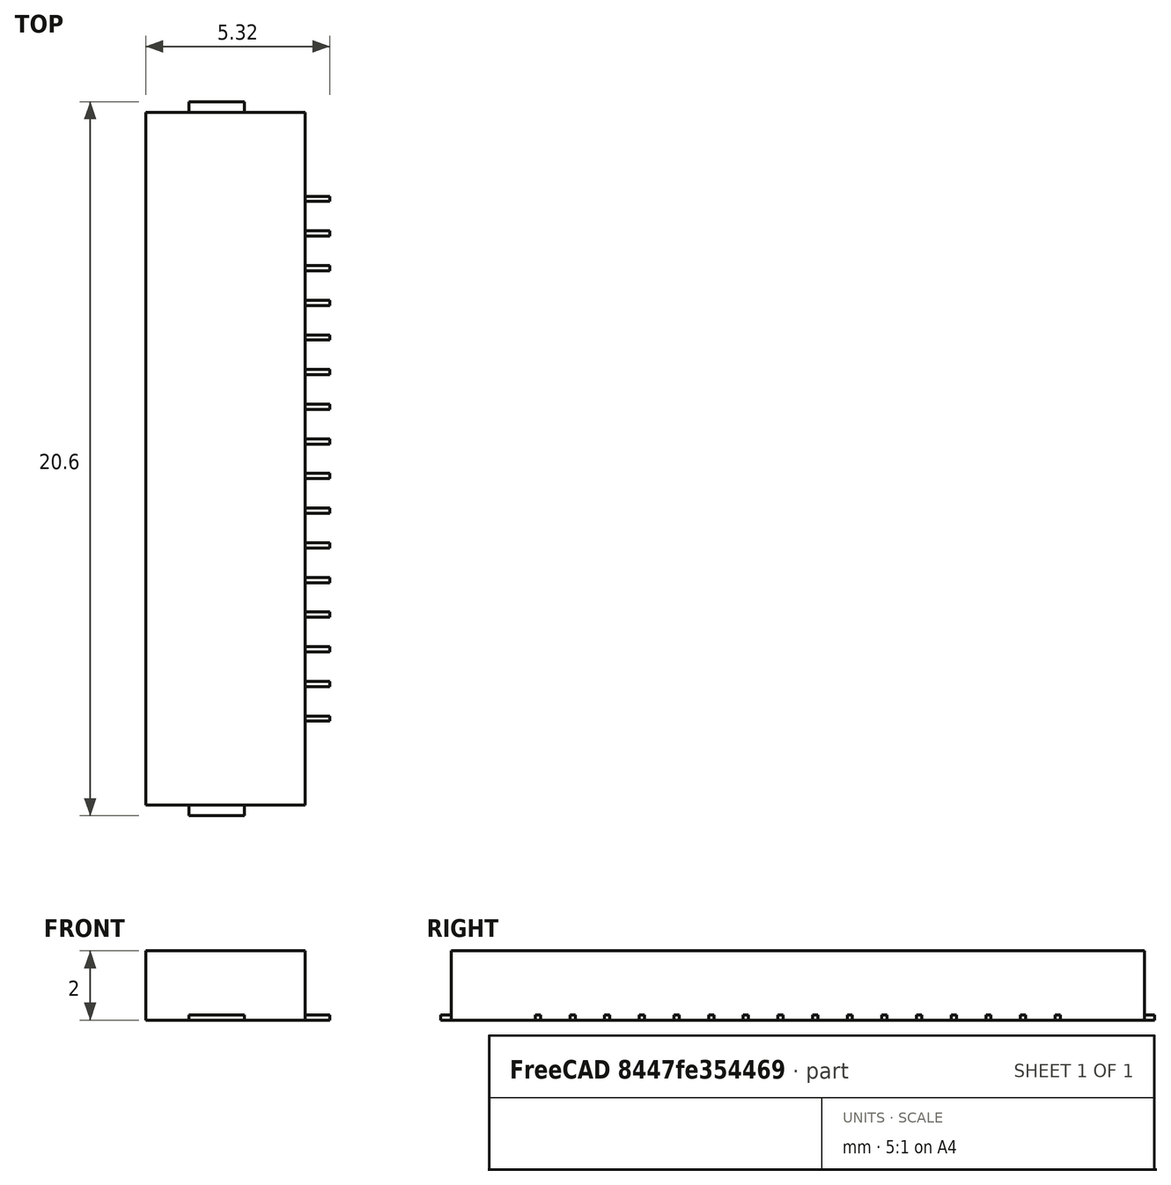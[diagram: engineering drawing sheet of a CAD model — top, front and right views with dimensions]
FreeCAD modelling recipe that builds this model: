
FCSTD DOCUMENT  (FreeCAD 0.20R29603 (Git))
Label: XFCN_F1004-H-16-20G-R
License: All rights reserved
LicenseURL: http://en.wikipedia.org/wiki/All_rights_reserved
objects: Part::Box×19
note: 19 computed .brp shape members not serialized (recipe doc carries the construction recipe); baked Part::Feature solids carry a one-line shape summary decoded from their .brp

FEATURE [Part::Box] Box  label="Body"
  AttacherType = Attacher::AttachEngine3D
  Height = 2
  Length = 4.6
  Width = 20
FEATURE [Part::Box] Box001  label="Pin 001"
  AttacherType = Attacher::AttachEngine3D
  Height = 0.15
  Length = 0.72
  Placement = pos=(4.6,17.425,0) rot=(0,0,1;0rad)
  Width = 0.15
FEATURE [Part::Box] Box002  label="Pin 002"
  AttacherType = Attacher::AttachEngine3D
  Height = 0.15
  Length = 0.72
  Placement = pos=(4.6,16.425,0) rot=(0,0,1;0rad)
  Width = 0.15
FEATURE [Part::Box] Box003  label="Pin 003"
  AttacherType = Attacher::AttachEngine3D
  Height = 0.15
  Length = 0.72
  Placement = pos=(4.6,15.425,0) rot=(0,0,1;0rad)
  Width = 0.15
FEATURE [Part::Box] Box004  label="Pin 004"
  AttacherType = Attacher::AttachEngine3D
  Height = 0.15
  Length = 0.72
  Placement = pos=(4.6,14.425,0) rot=(0,0,1;0rad)
  Width = 0.15
FEATURE [Part::Box] Box005  label="Pin 005"
  AttacherType = Attacher::AttachEngine3D
  Height = 0.15
  Length = 0.72
  Placement = pos=(4.6,13.425,0) rot=(0,0,1;0rad)
  Width = 0.15
FEATURE [Part::Box] Box006  label="Pin 006"
  AttacherType = Attacher::AttachEngine3D
  Height = 0.15
  Length = 0.72
  Placement = pos=(4.6,12.425,0) rot=(0,0,1;0rad)
  Width = 0.15
FEATURE [Part::Box] Box007  label="Pin 007"
  AttacherType = Attacher::AttachEngine3D
  Height = 0.15
  Length = 0.72
  Placement = pos=(4.6,11.425,0) rot=(0,0,1;0rad)
  Width = 0.15
FEATURE [Part::Box] Box008  label="Pin 008"
  AttacherType = Attacher::AttachEngine3D
  Height = 0.15
  Length = 0.72
  Placement = pos=(4.6,10.425,0) rot=(0,0,1;0rad)
  Width = 0.15
FEATURE [Part::Box] Box009  label="Pin 009"
  AttacherType = Attacher::AttachEngine3D
  Height = 0.15
  Length = 0.72
  Placement = pos=(4.6,9.425,0) rot=(0,0,1;0rad)
  Width = 0.15
FEATURE [Part::Box] Box010  label="Pin 010"
  AttacherType = Attacher::AttachEngine3D
  Height = 0.15
  Length = 0.72
  Placement = pos=(4.6,8.425,0) rot=(0,0,1;0rad)
  Width = 0.15
FEATURE [Part::Box] Box011  label="Pin 011"
  AttacherType = Attacher::AttachEngine3D
  Height = 0.15
  Length = 0.72
  Placement = pos=(4.6,7.425,0) rot=(0,0,1;0rad)
  Width = 0.15
FEATURE [Part::Box] Box012  label="Pin 012"
  AttacherType = Attacher::AttachEngine3D
  Height = 0.15
  Length = 0.72
  Placement = pos=(4.6,6.425,0) rot=(0,0,1;0rad)
  Width = 0.15
FEATURE [Part::Box] Box013  label="Pin 013"
  AttacherType = Attacher::AttachEngine3D
  Height = 0.15
  Length = 0.72
  Placement = pos=(4.6,5.425,0) rot=(0,0,1;0rad)
  Width = 0.15
FEATURE [Part::Box] Box014  label="Pin 014"
  AttacherType = Attacher::AttachEngine3D
  Height = 0.15
  Length = 0.72
  Placement = pos=(4.6,4.425,0) rot=(0,0,1;0rad)
  Width = 0.15
FEATURE [Part::Box] Box015  label="Pin 015"
  AttacherType = Attacher::AttachEngine3D
  Height = 0.15
  Length = 0.72
  Placement = pos=(4.6,3.425,0) rot=(0,0,1;0rad)
  Width = 0.15
FEATURE [Part::Box] Box016  label="Pin 016"
  AttacherType = Attacher::AttachEngine3D
  Height = 0.15
  Length = 0.72
  Placement = pos=(4.6,2.425,0) rot=(0,0,1;0rad)
  Width = 0.15
FEATURE [Part::Box] Box017  label="Left mounting"
  AttacherType = Attacher::AttachEngine3D
  Height = 0.15
  Length = 1.6
  Placement = pos=(1.25,-0.3,0) rot=(0,0,1;0rad)
  Width = 0.3
FEATURE [Part::Box] Box018  label="Right mounting"
  AttacherType = Attacher::AttachEngine3D
  Height = 0.15
  Length = 1.6
  Placement = pos=(1.25,20,0) rot=(0,0,1;0rad)
  Width = 0.3
